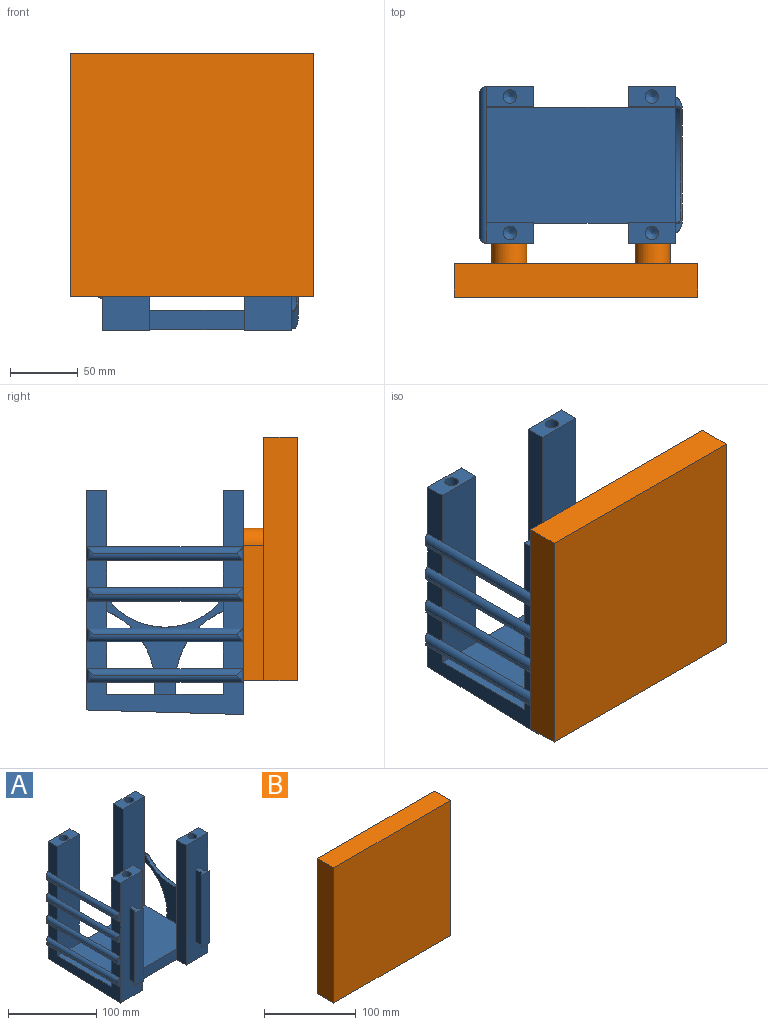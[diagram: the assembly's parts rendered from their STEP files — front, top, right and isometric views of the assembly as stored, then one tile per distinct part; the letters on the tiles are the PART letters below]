
ASSEMBLY  parts=2 mates=1
PART A: 97 faces, bbox 150.1x128.5x166 mm
  f0: plane 116x23.92mm, normal (-1,0,0), area 1811.5mm2, adj f1,f3,f14,f26,f30,f43,f96
  f1: plane 162.62x35mm, normal (0,1,0), area 5691.6mm2, adj f0,f7,f9,f11,f13,f17,f27,f41
  f2: plane 166x35mm, normal (0,-1,0), area 5310mm2, adj f21,f22,f29,f89,f93,f94,f95,f96
  f3: plane 166x35mm, normal (0,-1,0), area 5310mm2, adj f0,f8,f10,f12,f18,f19,f31,f42
  f4: plane 86x71.16mm, normal (-1,0,0), area 1534.7mm2, adj f14,f24,f28,f56,f57,f58,f65,f67
  f5: plane 82.36x71.32mm, normal (1,0,0), area 1229.1mm2, adj f59,f60,f61,f62,f63,f64,f66,f69
  f6: plane 164.29x57.01mm, normal (1,0,0), area 2884.9mm2, adj f14,f23,f24,f25,f57,f59,f60,f61
  f7: plane 19.9x15mm, normal (-1,0,0), area 298.5mm2, adj f1,f26,f40,f47
  f8: plane 19.9x15mm, normal (-1,0,0), area 298.5mm2, adj f3,f30,f40,f47
  f9: plane 19.9x15mm, normal (-1,0,0), area 298.5mm2, adj f1,f26,f44,f48
  f10: plane 19.9x15mm, normal (-1,0,0), area 298.5mm2, adj f3,f30,f44,f48
  f11: plane 19.9x15mm, normal (-1,0,0), area 298.5mm2, adj f1,f26,f51,f55
  f12: plane 19.9x15mm, normal (-1,0,0), area 298.5mm2, adj f3,f30,f51,f55
  f13: plane 41.98x15mm, normal (-1,0,0), area 629.6mm2, adj f1,f26,f27,f52
  f14: plane 140x86mm, normal (0,0,1), area 12040mm2, adj f0,f4,f6,f16,f20,f22,f24,f26
  f15: plane 163.06x15mm, normal (-1,0,0), area 2442.5mm2, adj f16,f23,f24,f25,f96
  f16: plane 70x12.06mm, normal (0,1,0), area 843.8mm2, adj f14,f15,f17,f96
  f17: plane 163.06x15mm, normal (1,0,0), area 2442.5mm2, adj f1,f16,f26,f27,f96
  f18: plane 41.98x15mm, normal (-1,0,0), area 629.6mm2, adj f3,f30,f31,f52
  f19: plane 166x15mm, normal (1,0,0), area 2486.7mm2, adj f3,f20,f30,f31,f96
  f20: plane 70x14.56mm, normal (0,-1,0), area 1019.4mm2, adj f14,f19,f21,f96
  f21: plane 166x15mm, normal (-1,0,0), area 2486.7mm2, adj f2,f20,f28,f29,f96
  f22: plane 166.01x57.05mm, normal (1,0,0), area 2983mm2, adj f2,f14,f28,f29,f58,f62,f63,f64
  f23: plane 162.62x35mm, normal (0,1,0), area 5691.6mm2, adj f6,f15,f25,f96
  f24: plane 151x35mm, normal (0,-1,0), area 5285mm2, adj f4,f6,f14,f15,f25
  f25: plane 35x15mm, normal (0,0,1), area 445.7mm2, adj f6,f15,f23,f24,f81
  f26: plane 151x35mm, normal (0,-1,0), area 5285mm2, adj f0,f7,f9,f11,f13,f14,f17,f27
  f27: plane 35x15mm, normal (0,0,1), area 445.7mm2, adj f1,f13,f17,f26,f79
  f28: plane 151x35mm, normal (0,1,0), area 5285mm2, adj f4,f14,f21,f22,f29
  f29: plane 35x15mm, normal (0,0,1), area 445.7mm2, adj f2,f21,f22,f28,f77
  f30: plane 151x35mm, normal (0,1,0), area 5285mm2, adj f0,f8,f10,f12,f14,f18,f19,f31
  f31: plane 35x15mm, normal (0,0,1), area 445.7mm2, adj f3,f18,f19,f30,f75
  f32: plane 86x10.1mm, normal (1,0,0), area 868.6mm2, adj f26,f30,f52,f55
  f33: plane 106x0.1mm, normal (-1,0,0), area 10.6mm2, adj f52,f53,f54,f55
  f34: plane 86x10.1mm, normal (1,0,0), area 868.6mm2, adj f26,f30,f48,f51
  f35: plane 106x0.1mm, normal (-1,0,0), area 10.6mm2, adj f48,f49,f50,f51
  f36: plane 86x10.1mm, normal (1,0,0), area 868.6mm2, adj f26,f30,f44,f47
  f37: plane 106x0.1mm, normal (-1,0,0), area 10.6mm2, adj f44,f45,f46,f47
  f38: plane 86x10.1mm, normal (1,0,0), area 868.6mm2, adj f26,f30,f40,f43
  f39: plane 106x0.1mm, normal (-1,0,0), area 10.6mm2, adj f40,f41,f42,f43
  f40: cylinder r=5mm len=116mm, axis (0,-1,0), area 882.5mm2, adj f7,f8,f38,f39,f41,f42
  f41: cylinder r=5mm len=10.1mm, axis (0,0,1), area 50.8mm2, adj f1,f39,f40,f43
  f42: cylinder r=5mm len=10.1mm, axis (0,0,-1), area 50.8mm2, adj f3,f39,f40,f43
  f43: cylinder r=5mm len=116mm, axis (0,1,0), area 882.5mm2, adj f0,f38,f39,f41,f42
  f44: cylinder r=5mm len=116mm, axis (0,-1,0), area 882.5mm2, adj f9,f10,f36,f37,f45,f46
  f45: cylinder r=5mm len=10.1mm, axis (0,0,1), area 50.8mm2, adj f1,f37,f44,f47
  f46: cylinder r=5mm len=10.1mm, axis (0,0,-1), area 50.8mm2, adj f3,f37,f44,f47
  f47: cylinder r=5mm len=116mm, axis (0,1,0), area 882.5mm2, adj f7,f8,f36,f37,f45,f46
  f48: cylinder r=5mm len=116mm, axis (0,1,0), area 882.5mm2, adj f9,f10,f34,f35,f49,f50
  f49: cylinder r=5mm len=10.1mm, axis (0,0,1), area 50.8mm2, adj f1,f35,f48,f51
  f50: cylinder r=5mm len=10.1mm, axis (0,0,-1), area 50.8mm2, adj f3,f35,f48,f51
  f51: cylinder r=5mm len=116mm, axis (0,-1,0), area 882.5mm2, adj f11,f12,f34,f35,f49,f50
  f52: cylinder r=5mm len=116mm, axis (0,-1,0), area 882.5mm2, adj f13,f18,f32,f33,f53,f54
  f53: cylinder r=5mm len=10.1mm, axis (0,0,1), area 50.8mm2, adj f1,f33,f52,f55
  f54: cylinder r=5mm len=10.1mm, axis (0,0,-1), area 50.8mm2, adj f3,f33,f52,f55
  f55: cylinder r=5mm len=116mm, axis (0,1,0), area 882.5mm2, adj f11,f12,f32,f33,f53,f54
  f56: cylinder r=53.61mm len=85.52mm, axis (1,0,0), area 387.4mm2, adj f4,f65,f66,f67
  f57: cylinder r=58.24mm len=62.35mm, axis (1,0,0), area 299.1mm2, adj f4,f6,f68,f69,f70
  f58: cylinder r=58.24mm len=62.35mm, axis (1,0,0), area 299.1mm2, adj f4,f22,f71,f72,f73
  f59: cylinder r=5mm len=9.62mm, axis (0,1,0), area 33.8mm2, adj f5,f6,f60,f65
  f60: cylinder r=5mm len=16.6mm, axis (0,-0.5,-0.87), area 73.6mm2, adj f5,f6,f59,f68
  f61: cylinder r=5mm len=20.01mm, axis (0,-0.5,-0.87), area 112.1mm2, adj f5,f6,f62,f70,f96
  f62: cylinder r=5mm len=20.01mm, axis (0,-0.5,0.87), area 112.3mm2, adj f5,f22,f61,f73,f96
  f63: cylinder r=5mm len=16.6mm, axis (0,-0.5,0.87), area 73.6mm2, adj f5,f22,f64,f71
  f64: cylinder r=5mm len=9.62mm, axis (0,1,0), area 33.8mm2, adj f5,f22,f63,f67
  f65: bspline ~5.77x5.59mm, area 9.4mm2, adj f4,f6,f56,f59,f66
  f66: torus R=54.61mm, axis (1,0,0), area 140.4mm2, adj f5,f56,f65,f67
  f67: bspline ~5.77x5.59mm, area 9.4mm2, adj f4,f22,f56,f64,f66
  f68: bspline ~8.91x5.52mm, area 10.1mm2, adj f6,f57,f60,f69
  f69: torus R=59.24mm, axis (1,0,0), area 100.9mm2, adj f5,f57,f68,f70
  f70: bspline ~9.34x5.52mm, area 10.1mm2, adj f6,f57,f61,f69
  f71: bspline ~8.91x5.52mm, area 10.1mm2, adj f22,f58,f63,f72
  f72: torus R=59.24mm, axis (1,0,0), area 100.9mm2, adj f5,f58,f71,f73
  f73: bspline ~9.34x5.52mm, area 10.1mm2, adj f22,f58,f62,f72
  f74: cone r=0mm half-angle=59deg, axis (0,0,1), area 92.5mm2, adj f75
  f75: cylinder r=5.03mm len=14mm, axis (0,0,1), area 442mm2, adj f31,f74
  f76: cone r=0mm half-angle=59deg, axis (0,0,1), area 92.5mm2, adj f77
  f77: cylinder r=5.03mm len=14mm, axis (0,0,1), area 442mm2, adj f29,f76
  f78: cone r=0mm half-angle=59deg, axis (0,0,1), area 92.5mm2, adj f79
  f79: cylinder r=5.03mm len=14mm, axis (0,0,1), area 442mm2, adj f27,f78
  f80: cone r=0mm half-angle=59deg, axis (0,0,1), area 92.5mm2, adj f81
  f81: cylinder r=5.03mm len=14mm, axis (0,0,1), area 442mm2, adj f25,f80
  f82: plane 100x8.5mm, normal (-1,0,0), area 850mm2, adj f3,f86,f87,f88
  f83: plane 100x8.5mm, normal (1,0,0), area 850mm2, adj f3,f84,f87,f88
  f84: plane 100x4mm, normal (0.71,0.71,0), area 565.7mm2, adj f83,f85,f87,f88
  f85: plane 100x13mm, normal (0,-1,0), area 1300mm2, adj f84,f86,f87,f88
  f86: plane 100x4mm, normal (-0.71,0.71,0), area 565.7mm2, adj f82,f85,f87,f88
  f87: plane 13x12.5mm, normal (0,0,1), area 78.5mm2, adj f3,f82,f83,f84,f85,f86
  f88: plane 13x12.5mm, normal (0,0,-1), area 78.5mm2, adj f3,f82,f83,f84,f85,f86
  f89: plane 100x8.5mm, normal (1,0,0), area 850mm2, adj f2,f90,f94,f95
  f90: plane 100x4mm, normal (0.71,0.71,0), area 565.7mm2, adj f89,f91,f94,f95
  f91: plane 100x13mm, normal (0,-1,0), area 1300mm2, adj f90,f92,f94,f95
  f92: plane 100x4mm, normal (-0.71,0.71,0), area 565.7mm2, adj f91,f93,f94,f95
  f93: plane 100x8.5mm, normal (-1,0,0), area 850mm2, adj f2,f92,f94,f95
  f94: plane 13x12.5mm, normal (0,0,1), area 78.5mm2, adj f2,f89,f90,f91,f92,f93
  f95: plane 13x12.5mm, normal (0,0,-1), area 78.5mm2, adj f2,f89,f90,f91,f92,f93
  f96: plane 142.78x116mm, normal (0,0.03,-1), area 14149.7mm2, adj f0,f1,f2,f3,f6,f15,f16,f17
PART B: 26 faces, bbox 180x40x180 mm
  f0: plane 180x180mm, normal (0,1,0), area 26669.1mm2, adj f1,f2,f3,f4,f8,f9,f20,f21
  f1: plane 180x25mm, normal (0,0,1), area 4500mm2, adj f0,f2,f4,f5
  f2: plane 180x25mm, normal (-1,0,0), area 4500mm2, adj f0,f1,f3,f5
  f3: plane 180x40mm, normal (0,0,-1), area 5123mm2, adj f0,f2,f4,f5,f6,f7,f8,f9
  f4: plane 180x25mm, normal (1,0,0), area 4500mm2, adj f0,f1,f3,f5
  f5: plane 180x180mm, normal (0,-1,0), area 32400mm2, adj f1,f2,f3,f4
  f6: plane 100x8.5mm, normal (-1,0,0), area 850mm2, adj f3,f7,f13,f25
  f7: plane 113x26mm, normal (0,1,0), area 2365.5mm2, adj f3,f6,f8,f9,f10,f24,f25
  f8: plane 100x15mm, normal (1,0,0), area 1500mm2, adj f0,f3,f7,f24
  f9: plane 100x15mm, normal (-1,0,0), area 1500mm2, adj f0,f3,f7,f24
  f10: plane 100x8.5mm, normal (1,0,0), area 850mm2, adj f3,f7,f11,f25
  f11: plane 100x4mm, normal (0.71,-0.71,0), area 565.7mm2, adj f3,f10,f12,f25
  f12: plane 100x13mm, normal (0,1,0), area 1300mm2, adj f3,f11,f13,f25
  f13: plane 100x4mm, normal (-0.71,-0.71,0), area 565.7mm2, adj f3,f6,f12,f25
  f14: plane 113x26mm, normal (0,1,0), area 2365.5mm2, adj f3,f15,f19,f20,f21,f22,f23
  f15: plane 100x8.5mm, normal (1,0,0), area 850mm2, adj f3,f14,f16,f22
  f16: plane 100x4mm, normal (0.71,-0.71,0), area 565.7mm2, adj f3,f15,f17,f22
  f17: plane 100x13mm, normal (0,1,0), area 1300mm2, adj f3,f16,f18,f22
  f18: plane 100x4mm, normal (-0.71,-0.71,0), area 565.7mm2, adj f3,f17,f19,f22
  f19: plane 100x8.5mm, normal (-1,0,0), area 850mm2, adj f3,f14,f18,f22
  f20: plane 100x15mm, normal (1,0,0), area 1500mm2, adj f0,f3,f14,f23
  f21: plane 100x15mm, normal (-1,0,0), area 1500mm2, adj f0,f3,f14,f23
  f22: plane 13x12.5mm, normal (0,0,-1), area 78.5mm2, adj f14,f15,f16,f17,f18,f19
  f23: cylinder r=13mm len=26mm, axis (0,-1,0), area 612.6mm2, adj f0,f14,f20,f21
  f24: cylinder r=13mm len=26mm, axis (0,-1,0), area 612.6mm2, adj f0,f7,f8,f9
  f25: plane 13x12.5mm, normal (0,0,-1), area 78.5mm2, adj f6,f7,f10,f11,f12,f13
PLACE A t=(-11.47,51.28,9.19)mm
PLACE B t=(-11.47,-21.72,109.19)mm
MATE slider B.f22 <-> A.f94  axis (0,0,-1) through (41.53,-13.97,119.19)mm
